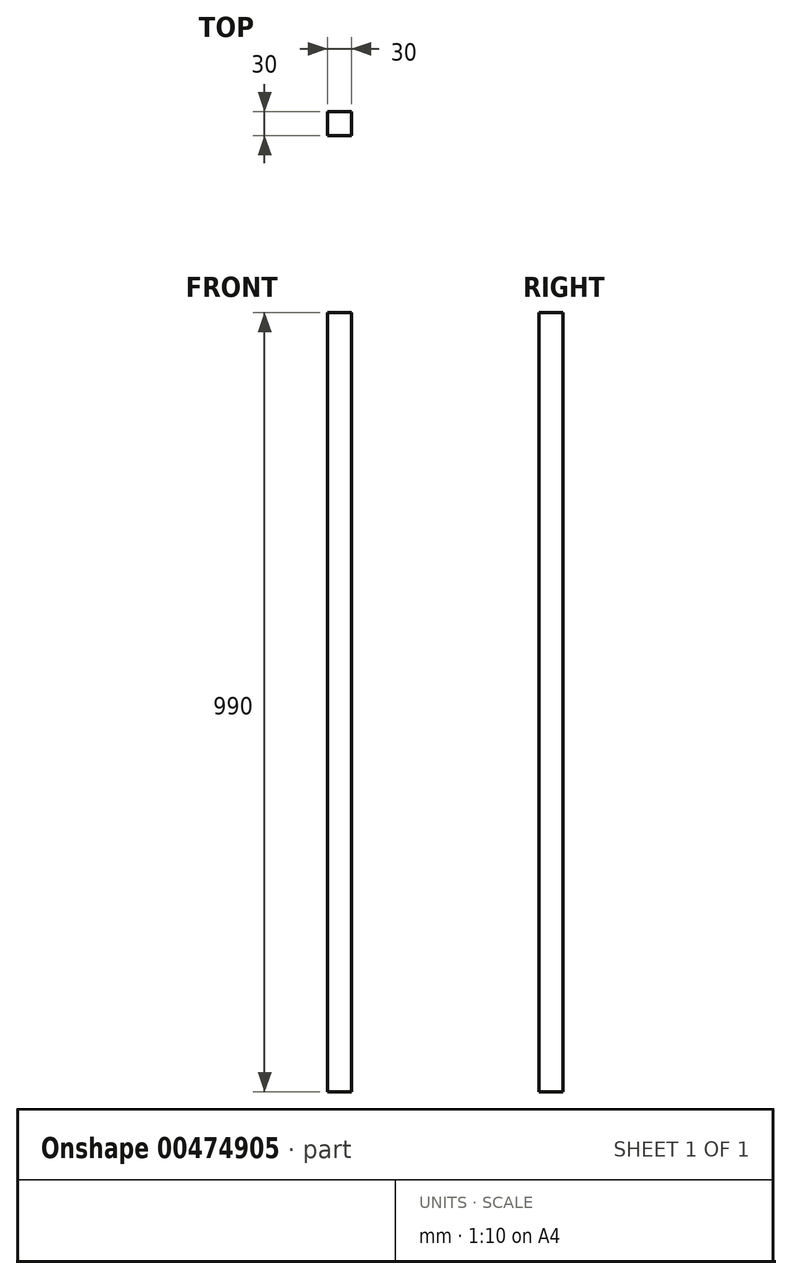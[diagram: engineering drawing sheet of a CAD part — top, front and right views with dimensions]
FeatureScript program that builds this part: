
annotation { "Feature Type Name" : "Feature", "Feature Type Description" : "" }
export const myFeature = defineFeature(function(context is Context, id is Id, definition is map)
    precondition{}
    {
        {
            var Q0;
            Q0=qCreatedBy(makeId("Front.planeOp"),FACE);
            var sketch = newSketch(context, id + "F0", { "sketchPlane" : qUnion([Q0])});
            skLineSegment(sketch, "E0.bottom", {"start": v(-59.04, 771.55) * mm, "end": v(-29.04, 771.55) * mm});
            skLineSegment(sketch, "E0.top", {"start": v(-59.04, -218.45) * mm, "end": v(-29.04, -218.45) * mm});
            skLineSegment(sketch, "E0.left", {"start": v(-59.04, 771.55) * mm, "end": v(-59.04, -218.45) * mm});
            skLineSegment(sketch, "E0.right", {"start": v(-29.04, 771.55) * mm, "end": v(-29.04, -218.45) * mm});
            skSolve(sketch);
        }
        {
            var Q0;
            Q0 = qSketchRegion(id + "F0", true);
            extrude(context, id + "F1", {"entities" : qUnion([Q0]), "depth" : 30 * mm});
        }
    });
